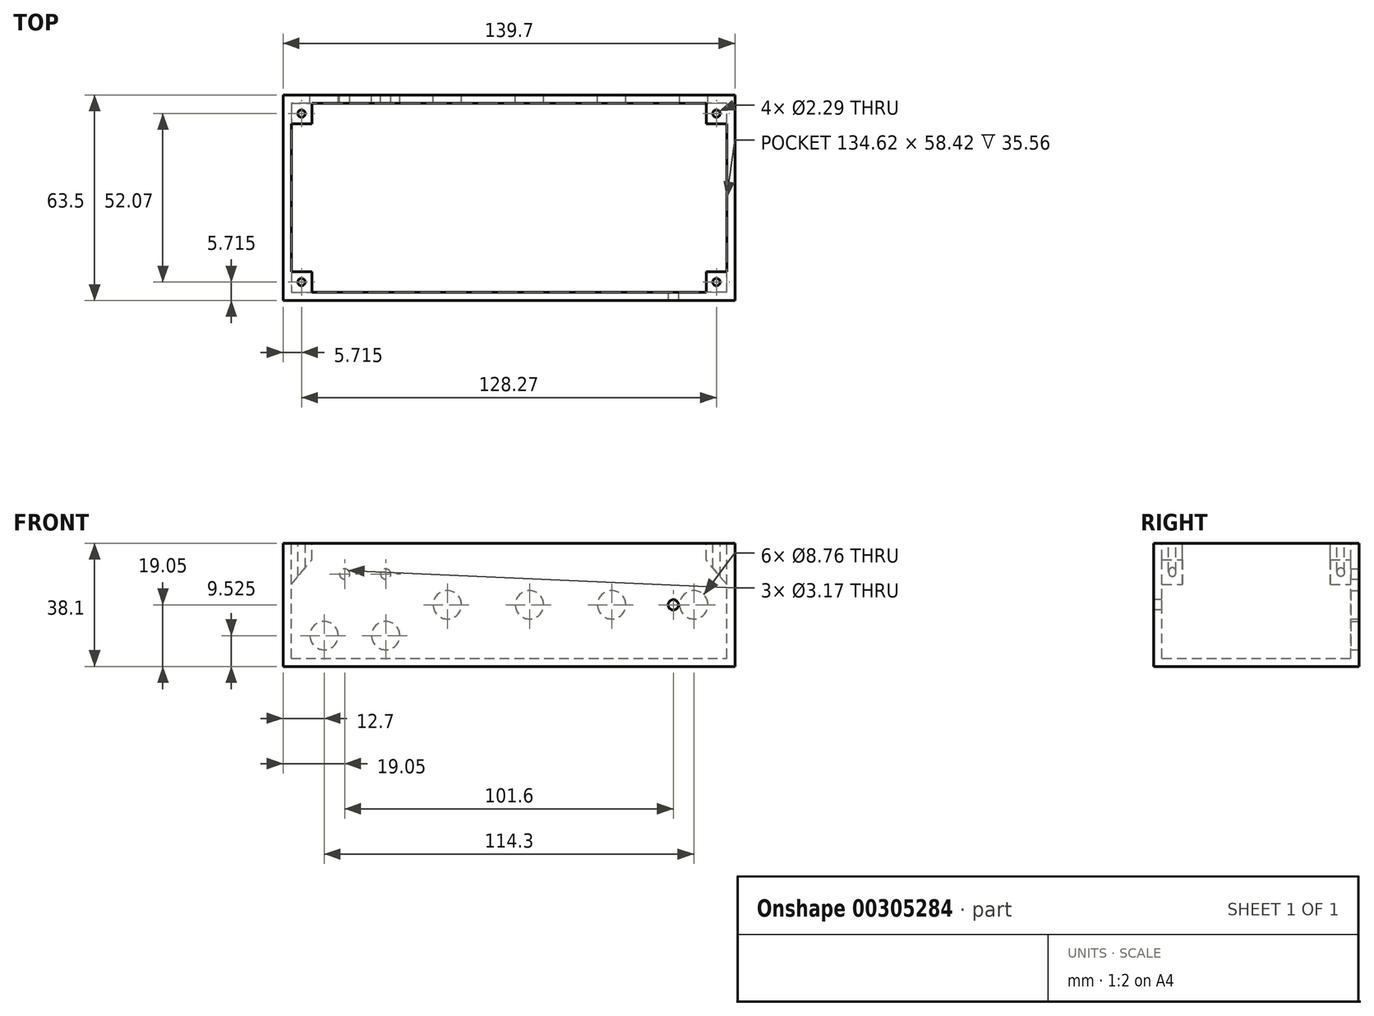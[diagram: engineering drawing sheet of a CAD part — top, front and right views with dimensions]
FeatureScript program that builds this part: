
annotation { "Feature Type Name" : "Feature", "Feature Type Description" : "" }
export const myFeature = defineFeature(function(context is Context, id is Id, definition is map)
    precondition{}
    {
        {
            var Q0;
            Q0=qCreatedBy(makeId("Top.planeOp"),FACE);
            var sketch = newSketch(context, id + "F0", { "sketchPlane" : qUnion([Q0])});
            skLineSegment(sketch, "E0.bottom", {"start": v(69.85, -31.75) * mm, "end": v(-69.85, -31.75) * mm});
            skLineSegment(sketch, "E0.top", {"start": v(69.85, 31.75) * mm, "end": v(-69.85, 31.75) * mm});
            skLineSegment(sketch, "E0.left", {"start": v(69.85, -31.75) * mm, "end": v(69.85, 31.75) * mm});
            skLineSegment(sketch, "E0.right", {"start": v(-69.85, -31.75) * mm, "end": v(-69.85, 31.75) * mm});
            skPoint(sketch, "E0.middle", {"position": v(0, 0) * mm});
            skSolve(sketch);
        }
        {
            var Q0;
            Q0 = qSketchRegion(id + "F0", true);
            extrude(context, id + "F1", {"entities" : qUnion([Q0]), "endBound" : BoundingType.SYMMETRIC, "depth" : 38.1 * mm});
        }
        {
            var Q0;
            Q0=makeQuery(id+"F1.opExtrude","CAP_FACE",FACE,{"disambiguationData":[OSD([sQuery(id+"F0.wireOp",EDGE,"E0.bottom"),sQuery(id+"F0.wireOp",EDGE,"E0.top"),sQuery(id+"F0.wireOp",EDGE,"E0.left"),sQuery(id+"F0.wireOp",EDGE,"E0.right")])],"isStart":false});
            var sketch = newSketch(context, id + "F2", { "sketchPlane" : qUnion([Q0])});
            skLineSegment(sketch, "E1.0", {"start": v(67.31, -29.2) * mm, "end": v(67.31, 29.21) * mm});
            skLineSegment(sketch, "E1.1", {"start": v(-67.31, -29.21) * mm, "end": v(67.31, -29.2) * mm});
            skLineSegment(sketch, "E1.2", {"start": v(-67.31, 29.2) * mm, "end": v(-67.31, -29.21) * mm});
            skLineSegment(sketch, "E1.3", {"start": v(67.31, 29.21) * mm, "end": v(-67.31, 29.2) * mm});
            skSolve(sketch);
        }
        {
            var Q0;
            Q0 = qSketchRegion(id + "F2", true);
            extrude(context, id + "F3", {"entities" : qUnion([Q0]), "operationType" : NewBodyOperationType.REMOVE, "oppositeDirection" : true, "depth" : 35.56 * mm});
        }
        {
            var Q0;
            Q0=makeQuery(id+"F1.opExtrude","SWEPT_FACE",FACE,{"disambiguationData":[OSD([sQuery(id+"F0.wireOp",EDGE,"E0.bottom")])]});
            var sketch = newSketch(context, id + "F4", { "sketchPlane" : qUnion([Q0])});
            skLineSegment(sketch, "E2", {"start": v(-69.85, 0) * mm, "end": v(69.85, 0) * mm, "construction": true});
            skCircle(sketch, "E3", {"center": v(50.8, 0) * mm, "radius": 1.59 * mm});
            skSolve(sketch);
        }
        {
            var Q0;
            Q0 = qSketchRegion(id + "F4", true);
            extrude(context, id + "F5", {"entities" : qUnion([Q0]), "operationType" : NewBodyOperationType.REMOVE, "endBound" : BoundingType.UP_TO_NEXT, "oppositeDirection" : true, "depth" : 25.4 * mm});
        }
        {
            var Q0;
            Q0=makeQuery(id+"F1.opExtrude","SWEPT_FACE",FACE,{"disambiguationData":[OSD([sQuery(id+"F0.wireOp",EDGE,"E0.top")])]});
            var sketch = newSketch(context, id + "F6", { "sketchPlane" : qUnion([Q0])});
            skLineSegment(sketch, "E4", {"start": v(-69.85, 0) * mm, "end": v(69.85, 0) * mm, "construction": true});
            skLineSegment(sketch, "E5", {"start": v(-69.85, 9.53) * mm, "end": v(69.85, 9.53) * mm, "construction": true});
            skLineSegment(sketch, "E6", {"start": v(-69.85, -9.53) * mm, "end": v(69.85, -9.53) * mm, "construction": true});
            skCircle(sketch, "E7", {"center": v(-57.15, 0) * mm, "radius": 4.38 * mm});
            skCircle(sketch, "E8", {"center": v(-31.75, 0) * mm, "radius": 4.38 * mm});
            skCircle(sketch, "E9", {"center": v(-6.35, 0) * mm, "radius": 4.38 * mm});
            skCircle(sketch, "E10", {"center": v(19.05, 0) * mm, "radius": 4.38 * mm});
            skCircle(sketch, "E11", {"center": v(50.8, 9.53) * mm, "radius": 1.59 * mm});
            skCircle(sketch, "E12", {"center": v(38.1, 9.53) * mm, "radius": 1.59 * mm});
            skCircle(sketch, "E13", {"center": v(57.15, -9.53) * mm, "radius": 4.38 * mm});
            skCircle(sketch, "E14", {"center": v(38.1, -9.53) * mm, "radius": 4.38 * mm});
            skSolve(sketch);
        }
        {
            var Q0;
            Q0=makeQuery(id+"F6.imprint","IMPRINT",FACE,{"disambiguationData":[TD([[makeQuery(id+"F6.imprint","IMPRINT",EDGE,{"derivedFrom":sQuery(id+"F6.wireOp",EDGE,"E8")}),1.0]])]});
            var Q1;
            Q1=makeQuery(id+"F6.imprint","IMPRINT",FACE,{"disambiguationData":[TD([[makeQuery(id+"F6.imprint","IMPRINT",EDGE,{"derivedFrom":sQuery(id+"F6.wireOp",EDGE,"E9")}),1.0]])]});
            var Q2;
            Q2=makeQuery(id+"F6.imprint","IMPRINT",FACE,{"disambiguationData":[TD([[makeQuery(id+"F6.imprint","IMPRINT",EDGE,{"derivedFrom":sQuery(id+"F6.wireOp",EDGE,"E10")}),1.0]])]});
            var Q3;
            Q3=makeQuery(id+"F6.imprint","IMPRINT",FACE,{"disambiguationData":[TD([[makeQuery(id+"F6.imprint","IMPRINT",EDGE,{"derivedFrom":sQuery(id+"F6.wireOp",EDGE,"E11")}),1.0]])]});
            var Q4;
            Q4=makeQuery(id+"F6.imprint","IMPRINT",FACE,{"disambiguationData":[TD([[makeQuery(id+"F6.imprint","IMPRINT",EDGE,{"derivedFrom":sQuery(id+"F6.wireOp",EDGE,"E12")}),1.0]])]});
            var Q5;
            Q5=makeQuery(id+"F6.imprint","IMPRINT",FACE,{"disambiguationData":[TD([[makeQuery(id+"F6.imprint","IMPRINT",EDGE,{"derivedFrom":sQuery(id+"F6.wireOp",EDGE,"E13")}),1.0]])]});
            var Q6;
            Q6=makeQuery(id+"F6.imprint","IMPRINT",FACE,{"disambiguationData":[TD([[makeQuery(id+"F6.imprint","IMPRINT",EDGE,{"derivedFrom":sQuery(id+"F6.wireOp",EDGE,"E14")}),1.0]])]});
            var Q7;
            Q7=makeQuery(id+"F6.imprint","IMPRINT",FACE,{"disambiguationData":[TD([[makeQuery(id+"F6.imprint","IMPRINT",EDGE,{"derivedFrom":sQuery(id+"F6.wireOp",EDGE,"E7")}),1.0]])]});
            extrude(context, id + "F7", {"entities" : qUnion([Q0, Q1, Q2, Q3, Q4, Q5, Q6, Q7]), "operationType" : NewBodyOperationType.REMOVE, "endBound" : BoundingType.UP_TO_NEXT, "oppositeDirection" : true, "depth" : 25.4 * mm});
        }
        {
            var Q0;
            Q0=makeQuery(id+"F1.opExtrude","CAP_FACE",FACE,{"disambiguationData":[OSD([sQuery(id+"F0.wireOp",EDGE,"E0.bottom"),sQuery(id+"F0.wireOp",EDGE,"E0.top"),sQuery(id+"F0.wireOp",EDGE,"E0.left"),sQuery(id+"F0.wireOp",EDGE,"E0.right")])],"isStart":false});
            var sketch = newSketch(context, id + "F8", { "sketchPlane" : qUnion([Q0])});
            skLineSegment(sketch, "E15.bottom", {"start": v(-67.31, 29.2) * mm, "end": v(-60.96, 29.2) * mm});
            skLineSegment(sketch, "E15.top", {"start": v(-67.31, 22.86) * mm, "end": v(-60.96, 22.86) * mm});
            skLineSegment(sketch, "E15.left", {"start": v(-67.31, 29.2) * mm, "end": v(-67.31, 22.86) * mm});
            skLineSegment(sketch, "E15.right", {"start": v(-60.96, 29.2) * mm, "end": v(-60.96, 22.86) * mm});
            skLineSegment(sketch, "E16", {"start": v(0, 29.21) * mm, "end": v(0, -29.21) * mm, "construction": true});
            skLineSegment(sketch, "E17", {"start": v(-67.31, 0) * mm, "end": v(67.31, 0) * mm, "construction": true});
            skLineSegment(sketch, "E18.MirrorCS", {"start": v(-60.96, -29.21) * mm, "end": v(-60.96, -22.86) * mm});
            skLineSegment(sketch, "E19.MirrorCS", {"start": v(-67.31, -29.21) * mm, "end": v(-67.31, -22.86) * mm});
            skLineSegment(sketch, "E20.MirrorCS", {"start": v(-67.31, -22.86) * mm, "end": v(-60.96, -22.86) * mm});
            skLineSegment(sketch, "E21.MirrorCS", {"start": v(-67.3, -29.21) * mm, "end": v(-60.96, -29.21) * mm});
            skLineSegment(sketch, "E22.MirrorCS", {"start": v(60.96, 29.2) * mm, "end": v(60.96, 22.86) * mm});
            skLineSegment(sketch, "E23.MirrorCS", {"start": v(67.31, 29.2) * mm, "end": v(60.96, 29.2) * mm});
            skLineSegment(sketch, "E24.MirrorCS", {"start": v(67.31, 22.86) * mm, "end": v(60.96, 22.86) * mm});
            skLineSegment(sketch, "E25.MirrorCS", {"start": v(67.31, 29.2) * mm, "end": v(67.31, 22.86) * mm});
            skLineSegment(sketch, "E26.MirrorCS", {"start": v(67.3, -29.21) * mm, "end": v(60.96, -29.21) * mm});
            skLineSegment(sketch, "E27.MirrorCS", {"start": v(67.31, -22.86) * mm, "end": v(60.96, -22.86) * mm});
            skLineSegment(sketch, "E28.MirrorCS", {"start": v(67.31, -29.21) * mm, "end": v(67.31, -22.86) * mm});
            skLineSegment(sketch, "E29.MirrorCS", {"start": v(60.96, -29.21) * mm, "end": v(60.96, -22.86) * mm});
            skSolve(sketch);
        }
        {
            var Q0;
            Q0=makeQuery(id+"F8.imprint","IMPRINT",FACE,{"disambiguationData":[TD([[makeQuery(id+"F8.imprint","IMPRINT",EDGE,{"derivedFrom":sQuery(id+"F8.wireOp",EDGE,"E18.MirrorCS")}),1.0]])]});
            var Q1;
            Q1=makeQuery(id+"F8.imprint","IMPRINT",FACE,{"disambiguationData":[TD([[makeQuery(id+"F8.imprint","IMPRINT",EDGE,{"derivedFrom":sQuery(id+"F8.wireOp",EDGE,"E22.MirrorCS")}),1.0]])]});
            var Q2;
            Q2=makeQuery(id+"F8.imprint","IMPRINT",FACE,{"disambiguationData":[TD([[makeQuery(id+"F8.imprint","IMPRINT",EDGE,{"derivedFrom":sQuery(id+"F8.wireOp",EDGE,"E26.MirrorCS")}),1.0]])]});
            var Q3;
            Q3=makeQuery(id+"F8.imprint","IMPRINT",FACE,{"disambiguationData":[TD([[makeQuery(id+"F8.imprint","IMPRINT",EDGE,{"derivedFrom":sQuery(id+"F8.wireOp",EDGE,"E15.bottom")}),1.0]])]});
            extrude(context, id + "F9", {"entities" : qUnion([Q0, Q1, Q2, Q3]), "operationType" : NewBodyOperationType.ADD, "oppositeDirection" : true, "depth" : 12.7 * mm});
        }
        {
            var Q0;
            Q0=makeQuery(id+"F9.opExtrude","CAP_EDGE",EDGE,{"disambiguationData":[OSD([sQuery(id+"F8.wireOp",EDGE,"E15.right")])],"isStart":false});
            var Q1;
            Q1=makeQuery(id+"F9.opExtrude","CAP_EDGE",EDGE,{"disambiguationData":[OSD([sQuery(id+"F8.wireOp",EDGE,"E29.MirrorCS")])],"isStart":false});
            chamfer(context, id + "F10", {"entities" : qUnion([Q0, Q1]), "chamferType" : ChamferType.OFFSET_ANGLE, "width" : 6.35 * mm, "oppositeDirection" : false, "angle" : 50 * degree, "tangentPropagation" : true});
        }
        {
            var Q0;
            Q0=makeQuery(id+"F9.opExtrude","CAP_EDGE",EDGE,{"disambiguationData":[OSD([sQuery(id+"F8.wireOp",EDGE,"E22.MirrorCS")])],"isStart":false});
            var Q1;
            Q1=makeQuery(id+"F9.opExtrude","CAP_EDGE",EDGE,{"disambiguationData":[OSD([sQuery(id+"F8.wireOp",EDGE,"E18.MirrorCS")])],"isStart":false});
            chamfer(context, id + "F11", {"entities" : qUnion([Q0, Q1]), "chamferType" : ChamferType.OFFSET_ANGLE, "width" : 6.35 * mm, "oppositeDirection" : true, "angle" : 50 * degree, "tangentPropagation" : true});
        }
        {
            var Q0;
            Q0=makeQuery(id+"F9.boolean.opBoolean","MERGE",FACE,{"derivedFrom":[makeQuery(id+"F1.opExtrude","CAP_FACE",FACE,{"disambiguationData":[OSD([sQuery(id+"F0.wireOp",EDGE,"E0.bottom"),sQuery(id+"F0.wireOp",EDGE,"E0.top"),sQuery(id+"F0.wireOp",EDGE,"E0.left"),sQuery(id+"F0.wireOp",EDGE,"E0.right")])],"isStart":false}),makeQuery(id+"F9.opExtrude","CAP_FACE",FACE,{"disambiguationData":[OSD([sQuery(id+"F8.wireOp",EDGE,"E15.bottom"),sQuery(id+"F8.wireOp",EDGE,"E15.top"),sQuery(id+"F8.wireOp",EDGE,"E15.left"),sQuery(id+"F8.wireOp",EDGE,"E15.right")])],"isStart":true}),makeQuery(id+"F9.opExtrude","CAP_FACE",FACE,{"disambiguationData":[OSD([sQuery(id+"F8.wireOp",EDGE,"E18.MirrorCS"),sQuery(id+"F8.wireOp",EDGE,"E19.MirrorCS"),sQuery(id+"F8.wireOp",EDGE,"E20.MirrorCS"),sQuery(id+"F8.wireOp",EDGE,"E21.MirrorCS")])],"isStart":true}),makeQuery(id+"F9.opExtrude","CAP_FACE",FACE,{"disambiguationData":[OSD([sQuery(id+"F8.wireOp",EDGE,"E22.MirrorCS"),sQuery(id+"F8.wireOp",EDGE,"E23.MirrorCS"),sQuery(id+"F8.wireOp",EDGE,"E24.MirrorCS"),sQuery(id+"F8.wireOp",EDGE,"E25.MirrorCS")])],"isStart":true}),makeQuery(id+"F9.opExtrude","CAP_FACE",FACE,{"disambiguationData":[OSD([sQuery(id+"F8.wireOp",EDGE,"E26.MirrorCS"),sQuery(id+"F8.wireOp",EDGE,"E27.MirrorCS"),sQuery(id+"F8.wireOp",EDGE,"E28.MirrorCS"),sQuery(id+"F8.wireOp",EDGE,"E29.MirrorCS")])],"isStart":true})]});
            var sketch = newSketch(context, id + "F12", { "sketchPlane" : qUnion([Q0])});
            skLineSegment(sketch, "E30", {"start": v(-67.31, 22.86) * mm, "end": v(-60.96, 29.2) * mm, "construction": true});
            skCircle(sketch, "E31", {"center": v(-64.14, 26.03) * mm, "radius": 1.14 * mm});
            skLineSegment(sketch, "E32", {"start": v(0, 29.21) * mm, "end": v(0, -29.21) * mm, "construction": true});
            skLineSegment(sketch, "E33", {"start": v(-67.31, 0) * mm, "end": v(67.31, 0) * mm, "construction": true});
            skCircle(sketch, "E34.MirrorC", {"center": v(64.14, 26.03) * mm, "radius": 1.14 * mm});
            skCircle(sketch, "E35.MirrorC", {"center": v(-64.14, -26.04) * mm, "radius": 1.14 * mm});
            skCircle(sketch, "E36.MirrorC", {"center": v(64.14, -26.04) * mm, "radius": 1.14 * mm});
            skSolve(sketch);
        }
        {
            var Q0;
            Q0 = qSketchRegion(id + "F12", true);
            extrude(context, id + "F13", {"entities" : qUnion([Q0]), "operationType" : NewBodyOperationType.REMOVE, "oppositeDirection" : true, "depth" : 12.7 * mm});
        }
    });
